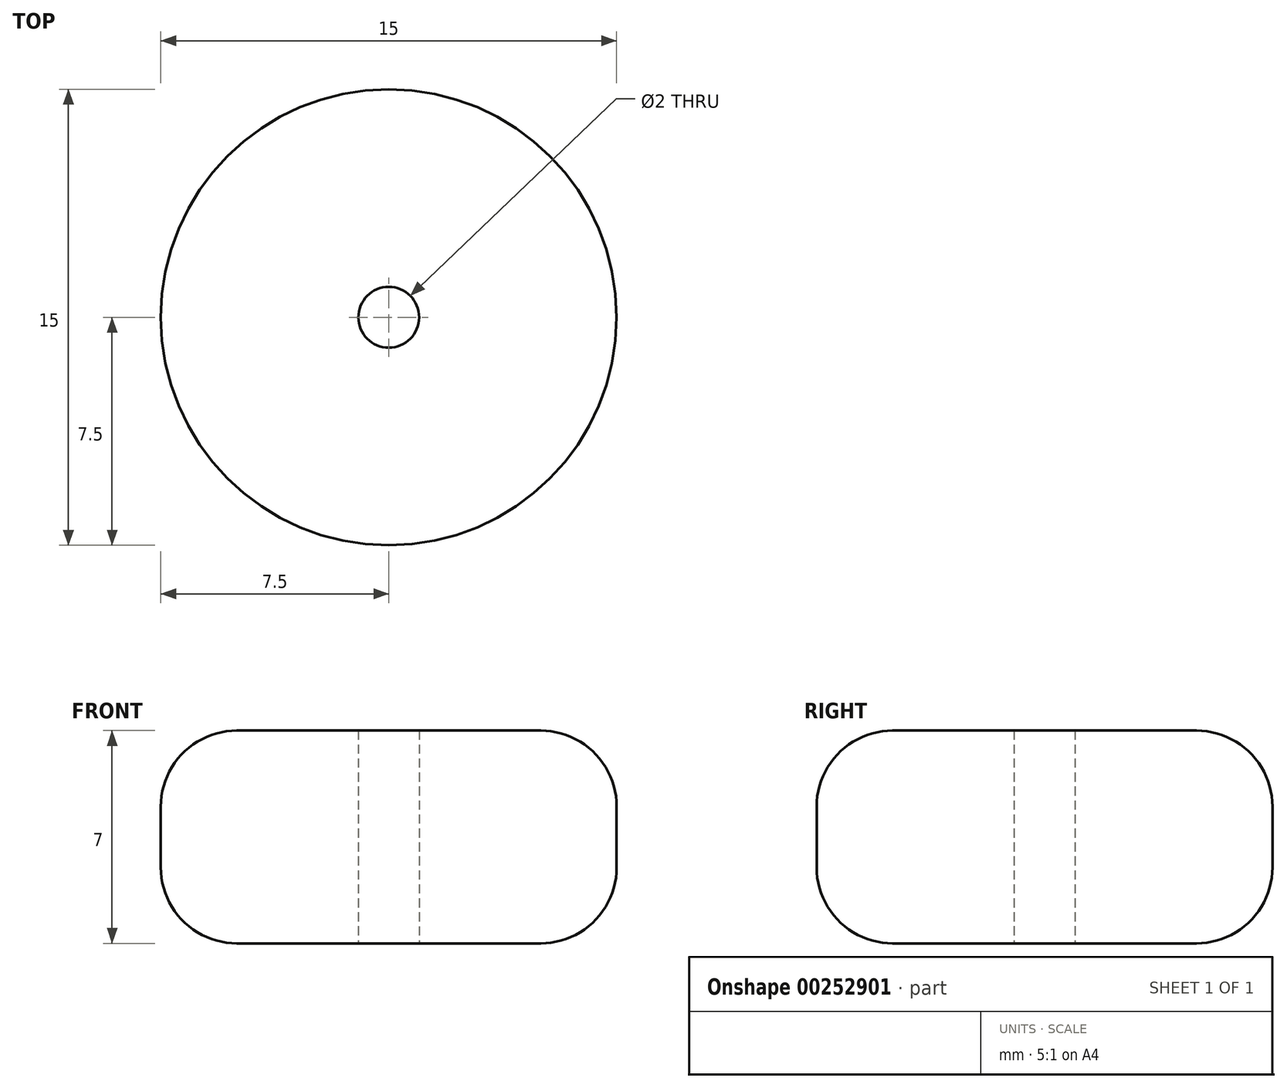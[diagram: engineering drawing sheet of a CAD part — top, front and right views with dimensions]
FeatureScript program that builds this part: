
annotation { "Feature Type Name" : "Feature", "Feature Type Description" : "" }
export const myFeature = defineFeature(function(context is Context, id is Id, definition is map)
    precondition{}
    {
        {
            var Q0;
            Q0=qCreatedBy(makeId("Top.planeOp"),FACE);
            var sketch = newSketch(context, id + "F0", { "sketchPlane" : qUnion([Q0])});
            skCircle(sketch, "E0", {"center": v(0, 0) * mm, "radius": 7.5 * mm});
            skCircle(sketch, "E1", {"center": v(0, 0) * mm, "radius": 1 * mm});
            skSolve(sketch);
        }
        {
            var Q0;
            Q0=makeQuery(id+"F0.imprint","IMPRINT",FACE,{"disambiguationData":[TD([[makeQuery(id+"F0.imprint","IMPRINT",EDGE,{"derivedFrom":sQuery(id+"F0.wireOp",EDGE,"E0")}),1.0]])]});
            extrude(context, id + "F1", {"entities" : qUnion([Q0]), "depth" : 7 * mm});
        }
        {
            var Q0;
            Q0=makeQuery(id+"F0.imprint","IMPRINT",FACE,{"disambiguationData":[TD([[makeQuery(id+"F0.imprint","IMPRINT",EDGE,{"derivedFrom":sQuery(id+"F0.wireOp",EDGE,"E0")}),1.0]])]});
            extrude(context, id + "F2", {"entities" : qUnion([Q0]), "operationType" : NewBodyOperationType.ADD, "depth" : 5 * mm});
        }
        {
            var Q0;
            Q0=makeQuery(id+"F1.opExtrude","CAP_EDGE",EDGE,{"disambiguationData":[OSD([sQuery(id+"F0.wireOp",EDGE,"E0")])],"isStart":false});
            var Q1;
            Q1=makeQuery(id+"F1.opExtrude","CAP_EDGE",EDGE,{"disambiguationData":[OSD([sQuery(id+"F0.wireOp",EDGE,"E0")])],"isStart":true});
            fillet(context, id + "F3", {"entities" : qUnion([Q0, Q1]), "radius" : 2.5 * mm, "tangentPropagation" : true, "allowEdgeOverflow" : false});
        }
    });
